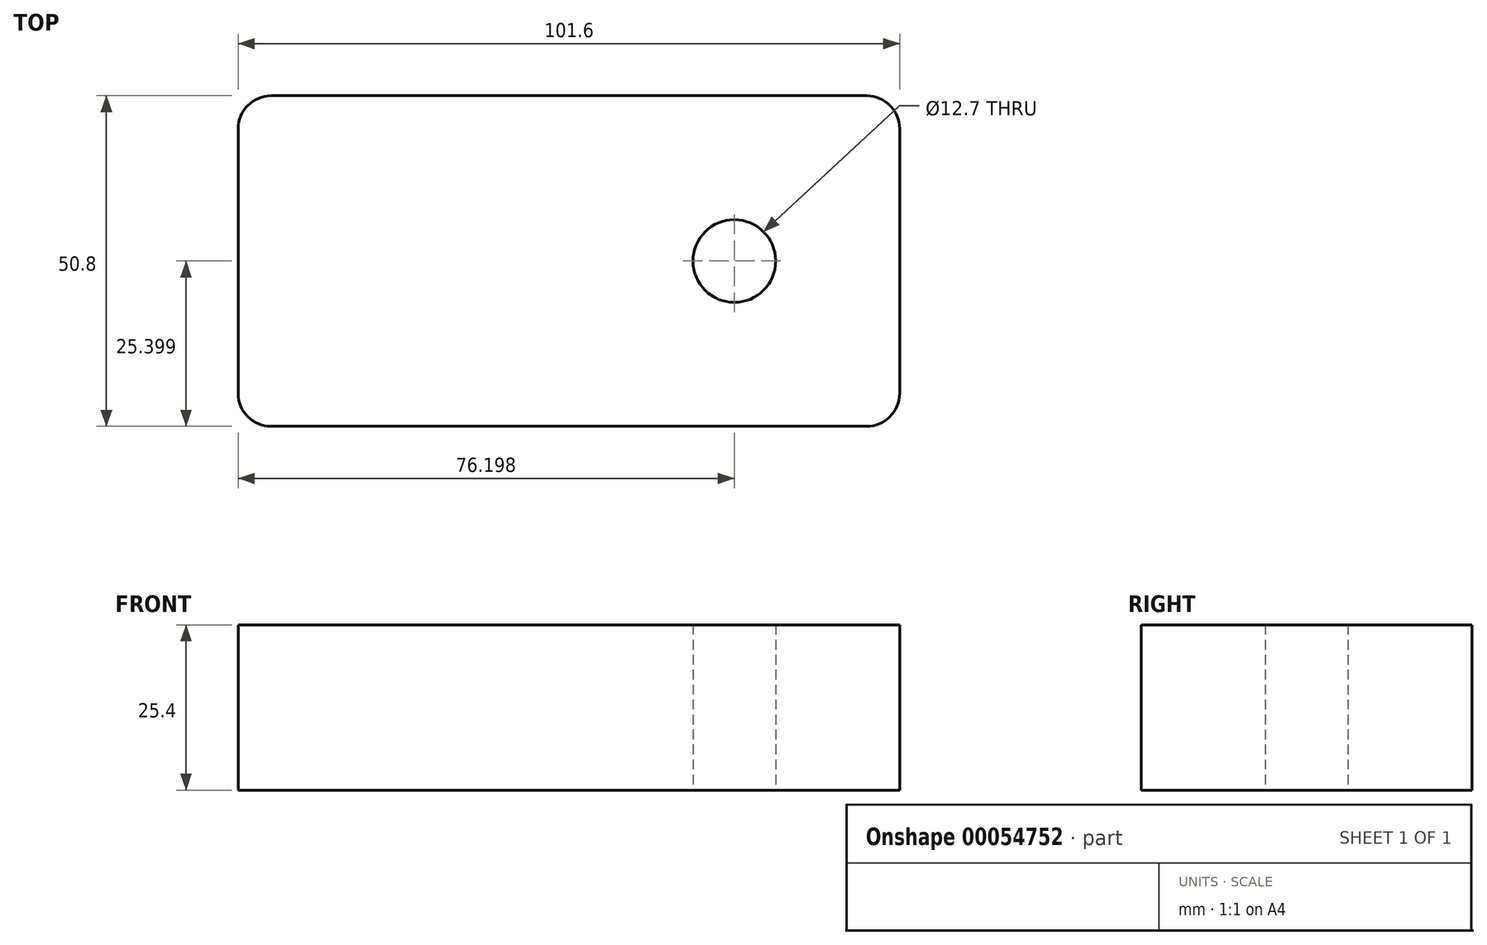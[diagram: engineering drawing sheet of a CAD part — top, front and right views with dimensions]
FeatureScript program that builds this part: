
annotation { "Feature Type Name" : "Feature", "Feature Type Description" : "" }
export const myFeature = defineFeature(function(context is Context, id is Id, definition is map)
    precondition{}
    {
        {
            var Q0;
            Q0=qCreatedBy(makeId("Top.planeOp"),FACE);
            var sketch = newSketch(context, id + "F0", { "sketchPlane" : qUnion([Q0])});
            skLineSegment(sketch, "E0.bottom", {"start": v(-51.13, 25.54) * mm, "end": v(50.47, 25.54) * mm});
            skLineSegment(sketch, "E0.top", {"start": v(-51.13, -25.26) * mm, "end": v(50.47, -25.26) * mm});
            skLineSegment(sketch, "E0.left", {"start": v(-51.13, 25.54) * mm, "end": v(-51.13, -25.26) * mm});
            skLineSegment(sketch, "E0.right", {"start": v(50.47, 25.54) * mm, "end": v(50.47, -25.26) * mm});
            skCircle(sketch, "E1", {"center": v(25.07, 0.14) * mm, "radius": 6.35 * mm});
            skSolve(sketch);
        }
        {
            var Q0;
            Q0 = qSketchRegion(id + "F0", true);
            extrude(context, id + "F1", {"entities" : qUnion([Q0]), "depth" : 25.4 * mm});
        }
        {
            var Q0;
            Q0=makeQuery(id+"F1.opExtrude","SWEPT_EDGE",EDGE,{"disambiguationData":[OSD([sQuery(id+"F0.wireOp",EDGE,"E0.top"),sQuery(id+"F0.wireOp",EDGE,"E0.right")])]});
            var Q1;
            Q1=makeQuery(id+"F1.opExtrude","SWEPT_EDGE",EDGE,{"disambiguationData":[OSD([sQuery(id+"F0.wireOp",EDGE,"E0.bottom"),sQuery(id+"F0.wireOp",EDGE,"E0.right")])]});
            var Q2;
            Q2=makeQuery(id+"F1.opExtrude","SWEPT_EDGE",EDGE,{"disambiguationData":[OSD([sQuery(id+"F0.wireOp",EDGE,"E0.top"),sQuery(id+"F0.wireOp",EDGE,"E0.left")])]});
            var Q3;
            Q3=makeQuery(id+"F1.opExtrude","SWEPT_EDGE",EDGE,{"disambiguationData":[OSD([sQuery(id+"F0.wireOp",EDGE,"E0.bottom"),sQuery(id+"F0.wireOp",EDGE,"E0.left")])]});
            fillet(context, id + "F2", {"entities" : qUnion([Q0, Q1, Q2, Q3]), "radius" : 5.08 * mm, "tangentPropagation" : true, "allowEdgeOverflow" : false});
        }
    });
